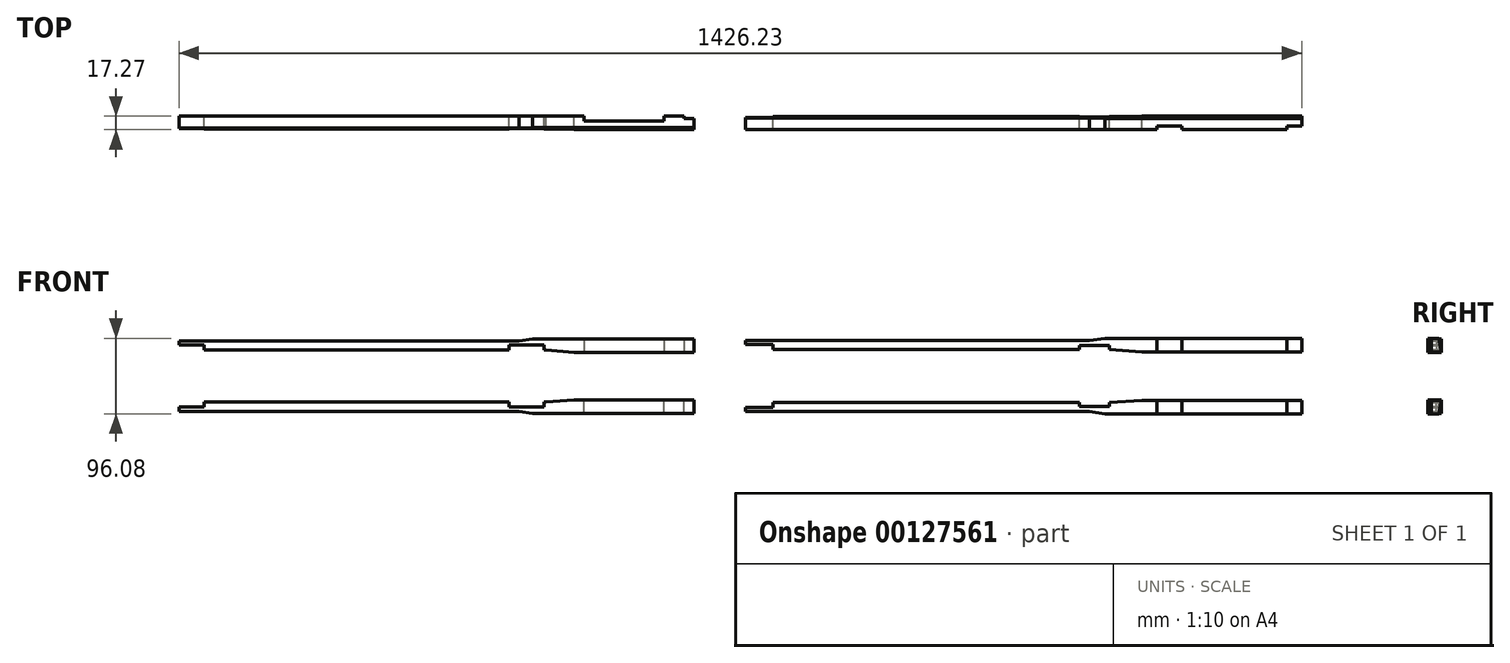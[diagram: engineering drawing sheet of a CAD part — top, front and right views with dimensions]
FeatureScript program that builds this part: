
annotation { "Feature Type Name" : "Feature", "Feature Type Description" : "" }
export const myFeature = defineFeature(function(context is Context, id is Id, definition is map)
    precondition{}
    {
        {
            var Q0;
            Q0=qCreatedBy(makeId("Front.planeOp"),FACE);
            var sketch = newSketch(context, id + "F0", { "sketchPlane" : qUnion([Q0])});
            skLineSegment(sketch, "E0", {"start": v(-536.89, -1.4) * mm, "end": v(-505.14, -1.4) * mm});
            skLineSegment(sketch, "E1", {"start": v(-117.79, -1.4) * mm, "end": v(-73.34, -1.4) * mm});
            skLineSegment(sketch, "E2", {"start": v(-505.14, -1.4) * mm, "end": v(-505.14, 4.95) * mm});
            skLineSegment(sketch, "E3", {"start": v(-117.79, -1.4) * mm, "end": v(-117.79, 4.95) * mm});
            skLineSegment(sketch, "E4", {"start": v(-73.34, -1.4) * mm, "end": v(-73.34, 4.95) * mm});
            skLineSegment(sketch, "E5", {"start": v(-505.14, 4.95) * mm, "end": v(-117.79, 4.95) * mm});
            skLineSegment(sketch, "E6", {"start": v(-73.34, 4.95) * mm, "end": v(-70.8, 4.95) * mm});
            skLineSegment(sketch, "E7", {"start": v(-22.54, 7.96) * mm, "end": v(117.16, 7.96) * mm});
            skLineSegment(sketch, "E8", {"start": v(-105.09, -6.74) * mm, "end": v(-536.89, -6.74) * mm});
            skLineSegment(sketch, "E9", {"start": v(-105.09, -6.74) * mm, "end": v(-87.45, -9.31) * mm});
            skLineSegment(sketch, "E10", {"start": v(-87.45, -9.31) * mm, "end": v(117.16, -9.31) * mm});
            skLineSegment(sketch, "E11", {"start": v(117.16, -9.31) * mm, "end": v(117.16, 7.96) * mm});
            skLineSegment(sketch, "E12", {"start": v(-536.89, -1.4) * mm, "end": v(-536.89, -6.74) * mm});
            skLineSegment(sketch, "E13", {"start": v(-22.54, 7.96) * mm, "end": v(-35.24, 7.96) * mm});
            skLineSegment(sketch, "E14", {"start": v(-35.24, 7.96) * mm, "end": v(-70.8, 4.95) * mm});
            skSolve(sketch);
        }
        {
            var Q0;
            Q0=makeQuery(id+"F0.imprint","IMPRINT",FACE,{"disambiguationData":[TD([[makeQuery(id+"F0.imprint","IMPRINT",EDGE,{"derivedFrom":sQuery(id+"F0.wireOp",EDGE,"E0")}),-1.0]])]});
            extrude(context, id + "F1", {"entities" : qUnion([Q0]), "depth" : 17.27 * mm});
        }
        {
            var Q0;
            Q0=makeQuery(id+"F1.opExtrude","SWEPT_FACE",FACE,{"disambiguationData":[OSD([sQuery(id+"F0.wireOp",EDGE,"E11")])]});
            var sketch = newSketch(context, id + "F2", { "sketchPlane" : qUnion([Q0])});
            skLineSegment(sketch, "E15", {"start": v(-17.27, 7.96) * mm, "end": v(-14.73, -9.31) * mm});
            skSolve(sketch);
        }
        {
            var Q0;
            Q0 = qSketchRegion(id + "F2", true);
            var Q1;
            {var subQ0=sQuery(id+"F2.wireOp",EDGE,"E15");Q1=makeQuery(id+"F2.imprint","IMPRINT",FACE,{"disambiguationData":[TD([[makeQuery(id+"F2.imprint","IMPRINT",EDGE,{"derivedFrom":subQ0}),-1.0]])]});}
            extrude(context, id + "F3", {"entities" : qUnion([Q0, Q1]), "operationType" : NewBodyOperationType.REMOVE, "oppositeDirection" : true, "depth" : 654.05 * mm});
        }
        {
            var Q0;
            Q0=makeQuery(id+"F1.opExtrude","SWEPT_FACE",FACE,{"disambiguationData":[OSD([sQuery(id+"F0.wireOp",EDGE,"E7")])]});
            var sketch = newSketch(context, id + "F4", { "sketchPlane" : qUnion([Q0])});
            skLineSegment(sketch, "E16.bottom", {"start": v(-22.54, 0) * mm, "end": v(79.06, 0) * mm});
            skLineSegment(sketch, "E16.top", {"start": v(-22.54, -6.35) * mm, "end": v(79.06, -6.35) * mm});
            skLineSegment(sketch, "E16.left", {"start": v(-22.54, 0) * mm, "end": v(-22.54, -6.35) * mm});
            skLineSegment(sketch, "E16.right", {"start": v(79.06, 0) * mm, "end": v(79.06, -6.35) * mm});
            skLineSegment(sketch, "E17.bottom", {"start": v(104.46, 0) * mm, "end": v(117.16, 0) * mm});
            skLineSegment(sketch, "E17.top", {"start": v(104.46, -3.18) * mm, "end": v(117.16, -3.18) * mm});
            skLineSegment(sketch, "E17.left", {"start": v(104.46, 0) * mm, "end": v(104.46, -3.18) * mm});
            skLineSegment(sketch, "E17.right", {"start": v(117.16, 0) * mm, "end": v(117.16, -3.18) * mm});
            skSolve(sketch);
        }
        {
            var Q0;
            Q0 = qSketchRegion(id + "F4", true);
            extrude(context, id + "F5", {"entities" : qUnion([Q0]), "operationType" : NewBodyOperationType.REMOVE, "oppositeDirection" : true, "depth" : 17.27 * mm});
        }
        {
            var Q0;
            Q0=makeQuery(id+"F1.opExtrude","SWEPT_BODY",BODY,{"disambiguationData":[OSD([sQuery(id+"F0.wireOp",EDGE,"E0"),sQuery(id+"F0.wireOp",EDGE,"E1"),sQuery(id+"F0.wireOp",EDGE,"E2"),sQuery(id+"F0.wireOp",EDGE,"E3"),sQuery(id+"F0.wireOp",EDGE,"E4"),sQuery(id+"F0.wireOp",EDGE,"E5"),sQuery(id+"F0.wireOp",EDGE,"E6"),sQuery(id+"F0.wireOp",EDGE,"E7"),sQuery(id+"F0.wireOp",EDGE,"E8"),sQuery(id+"F0.wireOp",EDGE,"E9"),sQuery(id+"F0.wireOp",EDGE,"E10"),sQuery(id+"F0.wireOp",EDGE,"E11"),sQuery(id+"F0.wireOp",EDGE,"E12"),sQuery(id+"F0.wireOp",EDGE,"E13"),sQuery(id+"F0.wireOp",EDGE,"E14")])]});
            transform(context, id + "F6", {"entities" : qUnion([Q0]), "transformType" : TransformType.TRANSLATION_3D, "dx" : 0 * mm, "dy" : 0 * mm, "dz" : 25.4 * mm, "makeCopy" : false});
        }
        {
            var Q0;
            Q0=makeQuery(id+"F1.opExtrude","SWEPT_BODY",BODY,{"disambiguationData":[OSD([sQuery(id+"F0.wireOp",EDGE,"E0"),sQuery(id+"F0.wireOp",EDGE,"E1"),sQuery(id+"F0.wireOp",EDGE,"E2"),sQuery(id+"F0.wireOp",EDGE,"E3"),sQuery(id+"F0.wireOp",EDGE,"E4"),sQuery(id+"F0.wireOp",EDGE,"E5"),sQuery(id+"F0.wireOp",EDGE,"E6"),sQuery(id+"F0.wireOp",EDGE,"E7"),sQuery(id+"F0.wireOp",EDGE,"E8"),sQuery(id+"F0.wireOp",EDGE,"E9"),sQuery(id+"F0.wireOp",EDGE,"E10"),sQuery(id+"F0.wireOp",EDGE,"E11"),sQuery(id+"F0.wireOp",EDGE,"E12"),sQuery(id+"F0.wireOp",EDGE,"E13"),sQuery(id+"F0.wireOp",EDGE,"E14")])]});
            var Q1;
            Q1=qCreatedBy(makeId("Top.planeOp"),FACE);
            mirror(context, id + "F7", {"entities" : qUnion([Q0]), "mirrorPlane" : qUnion([Q1])});
        }
        {
            var Q0;
            Q0=makeQuery(id+"F1.opExtrude","SWEPT_BODY",BODY,{"disambiguationData":[OSD([sQuery(id+"F0.wireOp",EDGE,"E0"),sQuery(id+"F0.wireOp",EDGE,"E1"),sQuery(id+"F0.wireOp",EDGE,"E2"),sQuery(id+"F0.wireOp",EDGE,"E3"),sQuery(id+"F0.wireOp",EDGE,"E4"),sQuery(id+"F0.wireOp",EDGE,"E5"),sQuery(id+"F0.wireOp",EDGE,"E6"),sQuery(id+"F0.wireOp",EDGE,"E7"),sQuery(id+"F0.wireOp",EDGE,"E8"),sQuery(id+"F0.wireOp",EDGE,"E9"),sQuery(id+"F0.wireOp",EDGE,"E10"),sQuery(id+"F0.wireOp",EDGE,"E11"),sQuery(id+"F0.wireOp",EDGE,"E12"),sQuery(id+"F0.wireOp",EDGE,"E13"),sQuery(id+"F0.wireOp",EDGE,"E14")])]});
            var Q1;
            Q1=makeQuery(id+"F7.opPattern","COPY",BODY,{"derivedFrom":makeQuery(id+"F1.opExtrude","SWEPT_BODY",BODY,{"disambiguationData":[OSD([sQuery(id+"F0.wireOp",EDGE,"E0"),sQuery(id+"F0.wireOp",EDGE,"E1"),sQuery(id+"F0.wireOp",EDGE,"E2"),sQuery(id+"F0.wireOp",EDGE,"E3"),sQuery(id+"F0.wireOp",EDGE,"E4"),sQuery(id+"F0.wireOp",EDGE,"E5"),sQuery(id+"F0.wireOp",EDGE,"E6"),sQuery(id+"F0.wireOp",EDGE,"E7"),sQuery(id+"F0.wireOp",EDGE,"E8"),sQuery(id+"F0.wireOp",EDGE,"E9"),sQuery(id+"F0.wireOp",EDGE,"E10"),sQuery(id+"F0.wireOp",EDGE,"E11"),sQuery(id+"F0.wireOp",EDGE,"E12"),sQuery(id+"F0.wireOp",EDGE,"E13"),sQuery(id+"F0.wireOp",EDGE,"E14")])]}),"instanceName":"1"});
            transform(context, id + "F8", {"entities" : qUnion([Q0, Q1]), "transformType" : TransformType.TRANSLATION_3D, "dx" : -152.4 * mm, "dy" : 0 * mm, "dz" : 0 * mm, "makeCopy" : false});
        }
        {
            var Q0;
            Q0=qCreatedBy(makeId("Front.planeOp"),FACE);
            var sketch = newSketch(context, id + "F9", { "sketchPlane" : qUnion([Q0])});
            skLineSegment(sketch, "E18", {"start": v(686.14, 28.16) * mm, "end": v(686.14, 45.43) * mm});
            skLineSegment(sketch, "E19", {"start": v(686.14, 45.43) * mm, "end": v(501.99, 45.43) * mm});
            skLineSegment(sketch, "E20", {"start": v(501.99, 45.43) * mm, "end": v(482.94, 45.43) * mm});
            skLineSegment(sketch, "E21", {"start": v(501.99, 28.16) * mm, "end": v(441.66, 28.16) * mm});
            skLineSegment(sketch, "E22", {"start": v(441.61, 42.38) * mm, "end": v(482.94, 45.43) * mm});
            skLineSegment(sketch, "E23", {"start": v(441.61, 42.38) * mm, "end": v(441.61, 37.62) * mm});
            skLineSegment(sketch, "E24", {"start": v(441.61, 37.62) * mm, "end": v(403.5, 37.62) * mm});
            skLineSegment(sketch, "E25", {"start": v(403.5, 37.62) * mm, "end": v(403.5, 42.38) * mm});
            skLineSegment(sketch, "E26", {"start": v(416.73, 31.3) * mm, "end": v(436.42, 28.16) * mm});
            skLineSegment(sketch, "E27", {"start": v(416.73, 31.3) * mm, "end": v(-20.6, 31.3) * mm});
            skLineSegment(sketch, "E28", {"start": v(-20.6, 31.3) * mm, "end": v(14.32, 31.3) * mm});
            skLineSegment(sketch, "E29", {"start": v(14.32, 42.38) * mm, "end": v(14.32, 36.07) * mm});
            skLineSegment(sketch, "E30", {"start": v(14.32, 36.07) * mm, "end": v(-20.58, 36.07) * mm});
            skLineSegment(sketch, "E31", {"start": v(14.32, 42.38) * mm, "end": v(403.5, 42.38) * mm});
            skLineSegment(sketch, "E32", {"start": v(436.42, 28.16) * mm, "end": v(441.66, 28.16) * mm});
            skLineSegment(sketch, "E33", {"start": v(501.99, 28.16) * mm, "end": v(686.14, 28.16) * mm});
            skLineSegment(sketch, "E34", {"start": v(-20.58, 36.07) * mm, "end": v(-20.6, 31.3) * mm});
            skSolve(sketch);
        }
        {
            var Q0;
            Q0 = qSketchRegion(id + "F9", true);
            extrude(context, id + "F10", {"entities" : qUnion([Q0]), "depth" : 17.27 * mm});
        }
        {
            var Q0;
            Q0=makeQuery(id+"F10.opExtrude","SWEPT_BODY",BODY,{"disambiguationData":[OSD([sQuery(id+"F9.wireOp",EDGE,"E18"),sQuery(id+"F9.wireOp",EDGE,"E19"),sQuery(id+"F9.wireOp",EDGE,"E20"),sQuery(id+"F9.wireOp",EDGE,"E21"),sQuery(id+"F9.wireOp",EDGE,"E22"),sQuery(id+"F9.wireOp",EDGE,"E23"),sQuery(id+"F9.wireOp",EDGE,"E24"),sQuery(id+"F9.wireOp",EDGE,"E25"),sQuery(id+"F9.wireOp",EDGE,"E26"),sQuery(id+"F9.wireOp",EDGE,"E27"),sQuery(id+"F9.wireOp",EDGE,"E28"),sQuery(id+"F9.wireOp",EDGE,"E29"),sQuery(id+"F9.wireOp",EDGE,"E30"),sQuery(id+"F9.wireOp",EDGE,"E31"),sQuery(id+"F9.wireOp",EDGE,"E32"),sQuery(id+"F9.wireOp",EDGE,"E33"),sQuery(id+"F9.wireOp",EDGE,"E34")])]});
            transform(context, id + "F11", {"entities" : qUnion([Q0]), "transformType" : TransformType.TRANSLATION_3D, "dx" : 50.8 * mm, "dy" : 0 * mm, "dz" : -12.7 * mm, "makeCopy" : false});
        }
        {
            var Q0;
            Q0=makeQuery(id+"F10.opExtrude","SWEPT_FACE",FACE,{"disambiguationData":[OSD([sQuery(id+"F9.wireOp",EDGE,"E21"),sQuery(id+"F9.wireOp",EDGE,"E32"),sQuery(id+"F9.wireOp",EDGE,"E33")])]});
            var sketch = newSketch(context, id + "F12", { "sketchPlane" : qUnion([Q0])});
            skLineSegment(sketch, "E35", {"start": v(736.94, 12.5) * mm, "end": v(717.89, 12.5) * mm});
            skLineSegment(sketch, "E36", {"start": v(717.89, 12.5) * mm, "end": v(717.89, 17.27) * mm});
            skLineSegment(sketch, "E37", {"start": v(584.54, 17.27) * mm, "end": v(584.54, 12.5) * mm});
            skLineSegment(sketch, "E38", {"start": v(584.54, 12.5) * mm, "end": v(552.79, 12.5) * mm});
            skLineSegment(sketch, "E39", {"start": v(552.79, 12.5) * mm, "end": v(552.79, 17.27) * mm});
            skLineSegment(sketch, "E40", {"start": v(552.79, 17.27) * mm, "end": v(584.54, 17.27) * mm});
            skLineSegment(sketch, "E41", {"start": v(717.89, 17.27) * mm, "end": v(736.94, 17.27) * mm});
            skLineSegment(sketch, "E42", {"start": v(736.94, 17.27) * mm, "end": v(736.94, 12.5) * mm});
            skSolve(sketch);
        }
        {
            var Q0;
            Q0 = qSketchRegion(id + "F12", true);
            extrude(context, id + "F13", {"entities" : qUnion([Q0]), "operationType" : NewBodyOperationType.REMOVE, "oppositeDirection" : true, "depth" : 17.27 * mm});
        }
        {
            var Q0;
            Q0=makeQuery(id+"F10.opExtrude","SWEPT_FACE",FACE,{"disambiguationData":[OSD([sQuery(id+"F9.wireOp",EDGE,"E18")])]});
            var sketch = newSketch(context, id + "F14", { "sketchPlane" : qUnion([Q0])});
            skLineSegment(sketch, "E43", {"start": v(0, 33.48) * mm, "end": v(-3.05, 15.46) * mm});
            skLineSegment(sketch, "E44", {"start": v(-3.05, 15.46) * mm, "end": v(0, 15.46) * mm});
            skLineSegment(sketch, "E45", {"start": v(0, 15.46) * mm, "end": v(0, 33.48) * mm});
            skSolve(sketch);
        }
        {
            var Q0;
            Q0 = qSketchRegion(id + "F14", true);
            extrude(context, id + "F15", {"entities" : qUnion([Q0]), "operationType" : NewBodyOperationType.REMOVE, "oppositeDirection" : true, "depth" : 711.2 * mm});
        }
        {
            var Q0;
            Q0=makeQuery(id+"F10.opExtrude","SWEPT_BODY",BODY,{"disambiguationData":[OSD([sQuery(id+"F9.wireOp",EDGE,"E18"),sQuery(id+"F9.wireOp",EDGE,"E19"),sQuery(id+"F9.wireOp",EDGE,"E20"),sQuery(id+"F9.wireOp",EDGE,"E21"),sQuery(id+"F9.wireOp",EDGE,"E22"),sQuery(id+"F9.wireOp",EDGE,"E23"),sQuery(id+"F9.wireOp",EDGE,"E24"),sQuery(id+"F9.wireOp",EDGE,"E25"),sQuery(id+"F9.wireOp",EDGE,"E26"),sQuery(id+"F9.wireOp",EDGE,"E27"),sQuery(id+"F9.wireOp",EDGE,"E28"),sQuery(id+"F9.wireOp",EDGE,"E29"),sQuery(id+"F9.wireOp",EDGE,"E30"),sQuery(id+"F9.wireOp",EDGE,"E31"),sQuery(id+"F9.wireOp",EDGE,"E32"),sQuery(id+"F9.wireOp",EDGE,"E33"),sQuery(id+"F9.wireOp",EDGE,"E34")])]});
            var Q1;
            Q1=qCreatedBy(makeId("Top.planeOp"),FACE);
            mirror(context, id + "F16", {"entities" : qUnion([Q0]), "mirrorPlane" : qUnion([Q1])});
        }
        {
            var Q0;
            Q0=makeQuery(id+"F7.opPattern","COPY",BODY,{"derivedFrom":makeQuery(id+"F1.opExtrude","SWEPT_BODY",BODY,{"disambiguationData":[OSD([sQuery(id+"F0.wireOp",EDGE,"E0"),sQuery(id+"F0.wireOp",EDGE,"E1"),sQuery(id+"F0.wireOp",EDGE,"E2"),sQuery(id+"F0.wireOp",EDGE,"E3"),sQuery(id+"F0.wireOp",EDGE,"E4"),sQuery(id+"F0.wireOp",EDGE,"E5"),sQuery(id+"F0.wireOp",EDGE,"E6"),sQuery(id+"F0.wireOp",EDGE,"E7"),sQuery(id+"F0.wireOp",EDGE,"E8"),sQuery(id+"F0.wireOp",EDGE,"E9"),sQuery(id+"F0.wireOp",EDGE,"E10"),sQuery(id+"F0.wireOp",EDGE,"E11"),sQuery(id+"F0.wireOp",EDGE,"E12"),sQuery(id+"F0.wireOp",EDGE,"E13"),sQuery(id+"F0.wireOp",EDGE,"E14")])]}),"instanceName":"1"});
            transform(context, id + "F17", {"entities" : qUnion([Q0]), "transformType" : TransformType.TRANSLATION_3D, "dx" : 0 * mm, "dy" : 0 * mm, "dz" : 127 * mm, "makeCopy" : false});
        }
        {
            var Q0;
            Q0=makeQuery(id+"F16.opPattern","COPY",BODY,{"derivedFrom":makeQuery(id+"F10.opExtrude","SWEPT_BODY",BODY,{"disambiguationData":[OSD([sQuery(id+"F9.wireOp",EDGE,"E18"),sQuery(id+"F9.wireOp",EDGE,"E19"),sQuery(id+"F9.wireOp",EDGE,"E20"),sQuery(id+"F9.wireOp",EDGE,"E21"),sQuery(id+"F9.wireOp",EDGE,"E22"),sQuery(id+"F9.wireOp",EDGE,"E23"),sQuery(id+"F9.wireOp",EDGE,"E24"),sQuery(id+"F9.wireOp",EDGE,"E25"),sQuery(id+"F9.wireOp",EDGE,"E26"),sQuery(id+"F9.wireOp",EDGE,"E27"),sQuery(id+"F9.wireOp",EDGE,"E28"),sQuery(id+"F9.wireOp",EDGE,"E29"),sQuery(id+"F9.wireOp",EDGE,"E30"),sQuery(id+"F9.wireOp",EDGE,"E31"),sQuery(id+"F9.wireOp",EDGE,"E32"),sQuery(id+"F9.wireOp",EDGE,"E33"),sQuery(id+"F9.wireOp",EDGE,"E34")])]}),"instanceName":"1"});
            transform(context, id + "F18", {"entities" : qUnion([Q0]), "transformType" : TransformType.TRANSLATION_3D, "dx" : 0 * mm, "dy" : 0 * mm, "dz" : 127 * mm, "makeCopy" : false});
        }
    });
